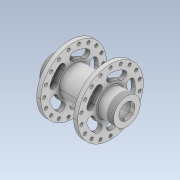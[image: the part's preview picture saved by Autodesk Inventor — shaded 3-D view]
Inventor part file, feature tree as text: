
AUTODESK INVENTOR PART (.ipt)
format: ipt  version: 2021 (Build 250183000, 183)  size: 443,392 bytes
history: native  units: mm
features: other x5, sketch x4, thread x3, revolve x2, extrude x2, fillet x2, pattern_circular x1, mirror x1
ambient origin geometry x8: Origin, YZ Plane, XZ Plane, XY Plane, X Axis, Y Axis, Z Axis, Center Point
bodies: Body1 (feature_tree), Body2 (feature_tree)
feature tree (20):
  other  "LlantaUser Library-Bike Weell.ipt"
  revolve  "Revolución1"  [1 undecoded]
  revolve  "Revolución3"  [1 undecoded]
  pattern_circular  "Patrón circular2"  Angle=90.0deg  [1 undecoded]
  mirror  "Simetría1"
  extrude  "Extrusión1"  Depth=60.0mm TaperAngle=360.0deg
  thread  "Rosca3"  [1 undecoded]
  thread  "Rosca4"  [1 undecoded]
  fillet  "Empalme2"  Radius=10.0mm
  extrude  "Extrusión2"  Depth=12.0mm TaperAngle=0.0deg
  fillet  "Empalme3"  Radius=1.0mm
  thread  "Rosca5"  [1 undecoded]
  other  "Solid1::LlantaUser Library-Bike Weell.ipt"
  other  "OperaciónIdentificador1"
  sketch  "Boceto1"  dims[d0=10.0mm d1=5.0mm]
  sketch  "Boceto3"  dims[d2=5.0mm d3=3.0mm]
  other  "Sólido3"
  sketch  "Boceto4"  dims[d4=90.0deg]
  sketch  "Boceto5"  dims[d5=4.0mm d10=90.0deg d11=60.0mm d12=360.0deg d19=1.5mm d20=8.0mm d21=0.0mm d22=10.0mm d23=0.0mm d24=12.0mm d25=0.0mm d26=1.0mm d27=1.5mm d28=8.0mm d29=0.0mm d30=1.0mm d31=8.0mm d32=0.0mm]
  other  "Sólido1"
note: 6 required parameter values undecoded (feature->parameter linkage not recoverable at this tier; creation-order binding heuristic only, values carry confidence <= 0.55)